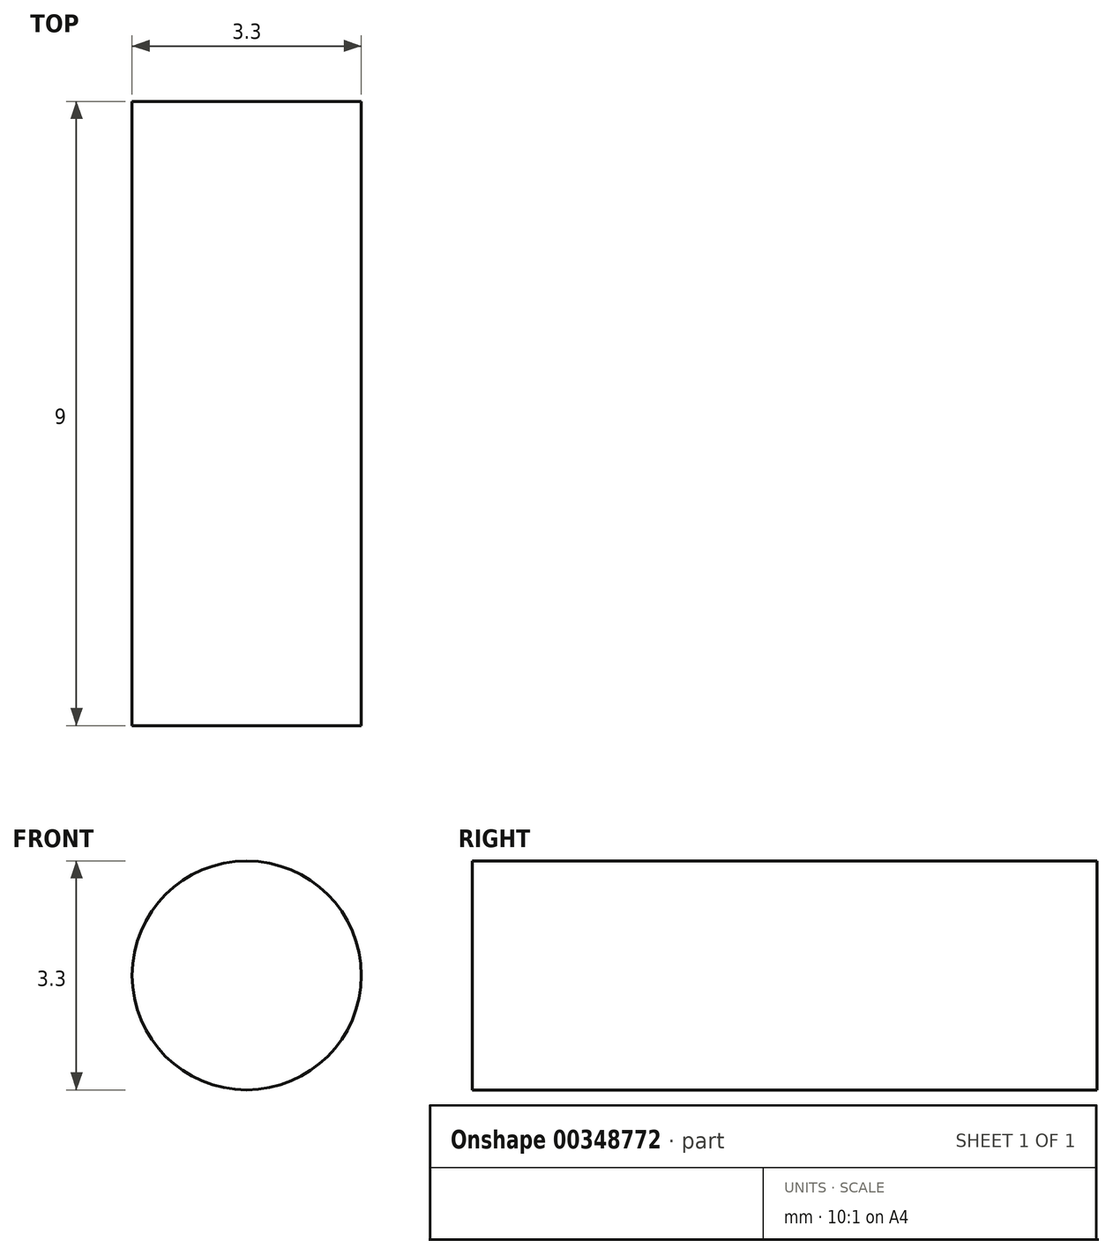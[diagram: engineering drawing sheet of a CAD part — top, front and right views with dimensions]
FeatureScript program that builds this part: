
annotation { "Feature Type Name" : "Feature", "Feature Type Description" : "" }
export const myFeature = defineFeature(function(context is Context, id is Id, definition is map)
    precondition{}
    {
        {
            var Q0;
            Q0=qCreatedBy(makeId("Top.planeOp"),FACE);
            var sketch = newSketch(context, id + "F0", { "sketchPlane" : qUnion([Q0])});
            skArc(sketch, "E0", {"start": v(3.1, 0) * mm, "mid": v(2.2, 2.2) * mm, "end": v(0, 3.1) * mm});
            skLineSegment(sketch, "E1", {"start": v(3.1, -3.1) * mm, "end": v(15, -3.1) * mm});
            skLineSegment(sketch, "E2", {"start": v(15, -3.1) * mm, "end": v(15, 5.9) * mm});
            skLineSegment(sketch, "E3", {"start": v(15, 5.9) * mm, "end": v(0, 5.9) * mm});
            skLineSegment(sketch, "E4", {"start": v(3.1, 0) * mm, "end": v(3.1, -3.1) * mm});
            skPoint(sketch, "E5.orphan", {"position": v(0, -3.1) * mm});
            skArc(sketch, "E6.MirrorCS", {"start": v(-3.1, 0) * mm, "mid": v(-2.2, 2.2) * mm, "end": v(0, 3.1) * mm});
            skLineSegment(sketch, "E7.MirrorCS", {"start": v(-3.1, 0) * mm, "end": v(-3.1, -3.1) * mm});
            skLineSegment(sketch, "E8.MirrorCS", {"start": v(-15, 5.9) * mm, "end": v(0, 5.9) * mm});
            skLineSegment(sketch, "E9.MirrorCS", {"start": v(-15, -3.1) * mm, "end": v(-15, 5.9) * mm});
            skLineSegment(sketch, "E10.MirrorCS", {"start": v(-3.1, -3.1) * mm, "end": v(-15, -3.1) * mm});
            skPoint(sketch, "E11.MirrorCS.end.orphan", {"position": v(0, 3.1) * mm});
            skPoint(sketch, "E11.MirrorCS.start.orphan", {"position": v(0, 5.9) * mm});
            skSolve(sketch);
        }
        {
            var Q0;
            Q0=makeQuery(id+"F0.imprint","IMPRINT",FACE,{"disambiguationData":[TD([[makeQuery(id+"F0.imprint","IMPRINT",EDGE,{"derivedFrom":sQuery(id+"F0.wireOp",EDGE,"E0")}),-1.0]])]});
            extrude(context, id + "F1", {"entities" : qUnion([Q0]), "depth" : 7 * mm});
        }
        {
            var Q0;
            Q0=makeQuery(id+"F1.opExtrude","SWEPT_FACE",FACE,{"disambiguationData":[OSD([sQuery(id+"F0.wireOp",EDGE,"E3"),sQuery(id+"F0.wireOp",EDGE,"E8.MirrorCS")])]});
            var sketch = newSketch(context, id + "F2", { "sketchPlane" : qUnion([Q0])});
            skLineSegment(sketch, "E12", {"start": v(15, 3.5) * mm, "end": v(-15, 3.5) * mm, "construction": true});
            skCircle(sketch, "E13", {"center": v(11.3, 3.5) * mm, "radius": 1.65 * mm});
            skCircle(sketch, "E14.MirrorC", {"center": v(-11.3, 3.5) * mm, "radius": 1.65 * mm});
            skSolve(sketch);
        }
        {
            var Q0;
            Q0=makeQuery(id+"F2.imprint","IMPRINT",FACE,{"disambiguationData":[TD([[makeQuery(id+"F2.imprint","IMPRINT",EDGE,{"derivedFrom":sQuery(id+"F2.wireOp",EDGE,"E13")}),1.0]])]});
            var Q1;
            Q1=makeQuery(id+"F2.imprint","IMPRINT",FACE,{"disambiguationData":[TD([[makeQuery(id+"F2.imprint","IMPRINT",EDGE,{"derivedFrom":sQuery(id+"F2.wireOp",EDGE,"E14.MirrorC")}),-1.0]])]});
            extrude(context, id + "F3", {"entities" : qUnion([Q0, Q1]), "operationType" : NewBodyOperationType.REMOVE, "endBound" : BoundingType.THROUGH_ALL, "oppositeDirection" : true, "depth" : 25 * mm});
        }
    });
